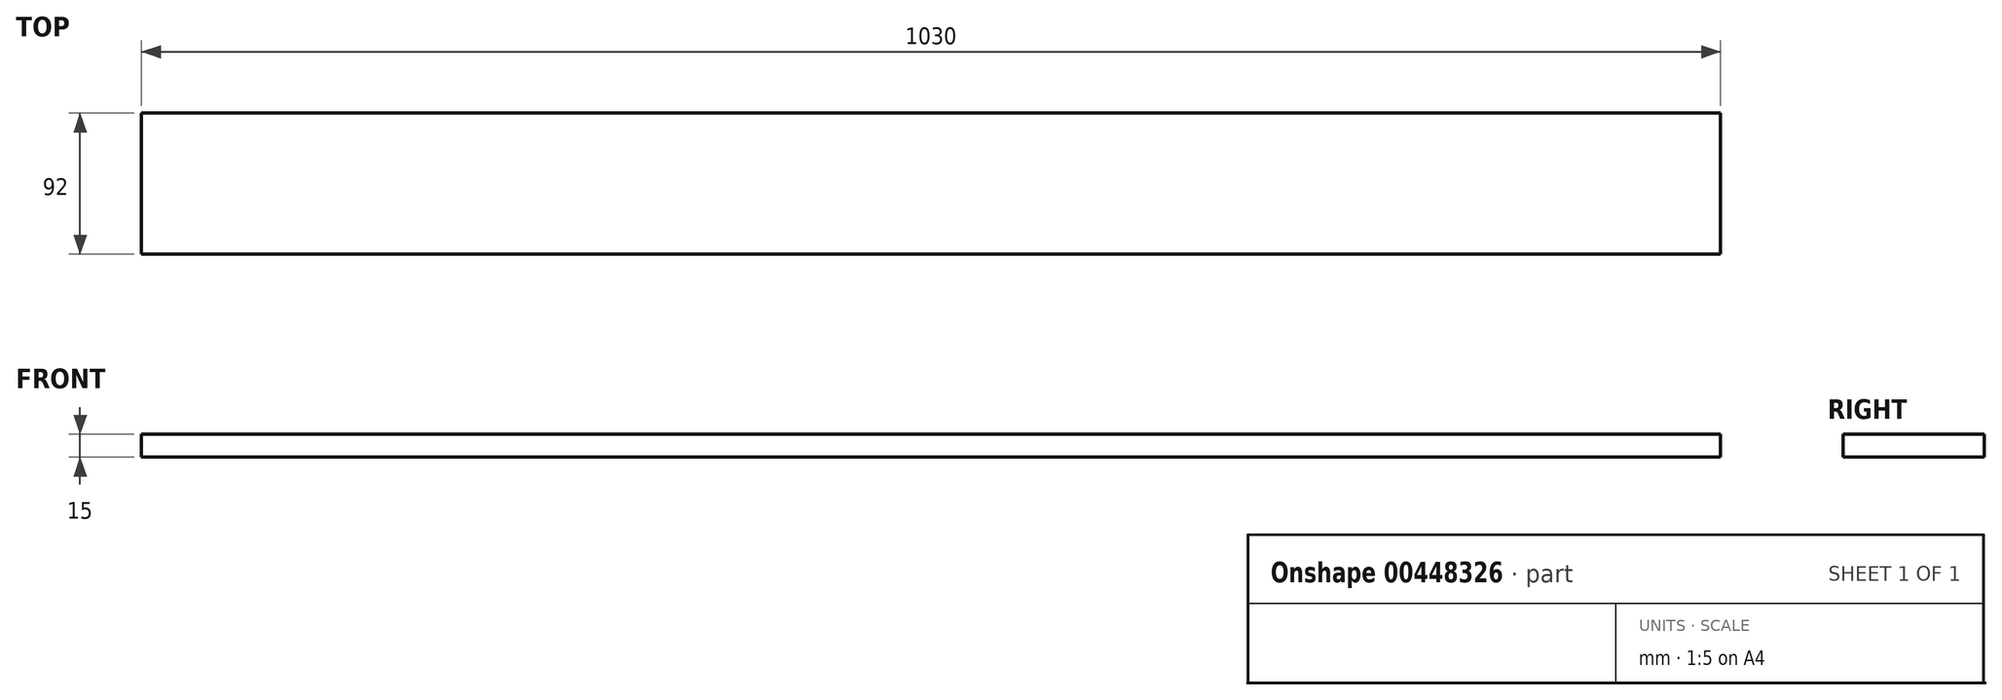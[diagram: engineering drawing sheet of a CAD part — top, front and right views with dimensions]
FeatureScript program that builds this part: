
annotation { "Feature Type Name" : "Feature", "Feature Type Description" : "" }
export const myFeature = defineFeature(function(context is Context, id is Id, definition is map)
    precondition{}
    {
        {
            var Q0;
            Q0=qCreatedBy(makeId("Top.planeOp"),FACE);
            var sketch = newSketch(context, id + "F0", { "sketchPlane" : qUnion([Q0])});
            skLineSegment(sketch, "E0.bottom", {"start": v(0, 0) * mm, "end": v(1030, 0) * mm});
            skLineSegment(sketch, "E0.top", {"start": v(0, 92) * mm, "end": v(1030, 92) * mm});
            skLineSegment(sketch, "E0.left", {"start": v(0, 0) * mm, "end": v(0, 92) * mm});
            skLineSegment(sketch, "E0.right", {"start": v(1030, 0) * mm, "end": v(1030, 92) * mm});
            skSolve(sketch);
        }
        {
            var Q0;
            Q0=makeQuery(id+"F0.imprint","IMPRINT",FACE,{"disambiguationData":[TD([[makeQuery(id+"F0.imprint","IMPRINT",EDGE,{"derivedFrom":sQuery(id+"F0.wireOp",EDGE,"E0.bottom")}),1.0]])]});
            extrude(context, id + "F1", {"entities" : qUnion([Q0]), "depth" : 15 * mm});
        }
    });
